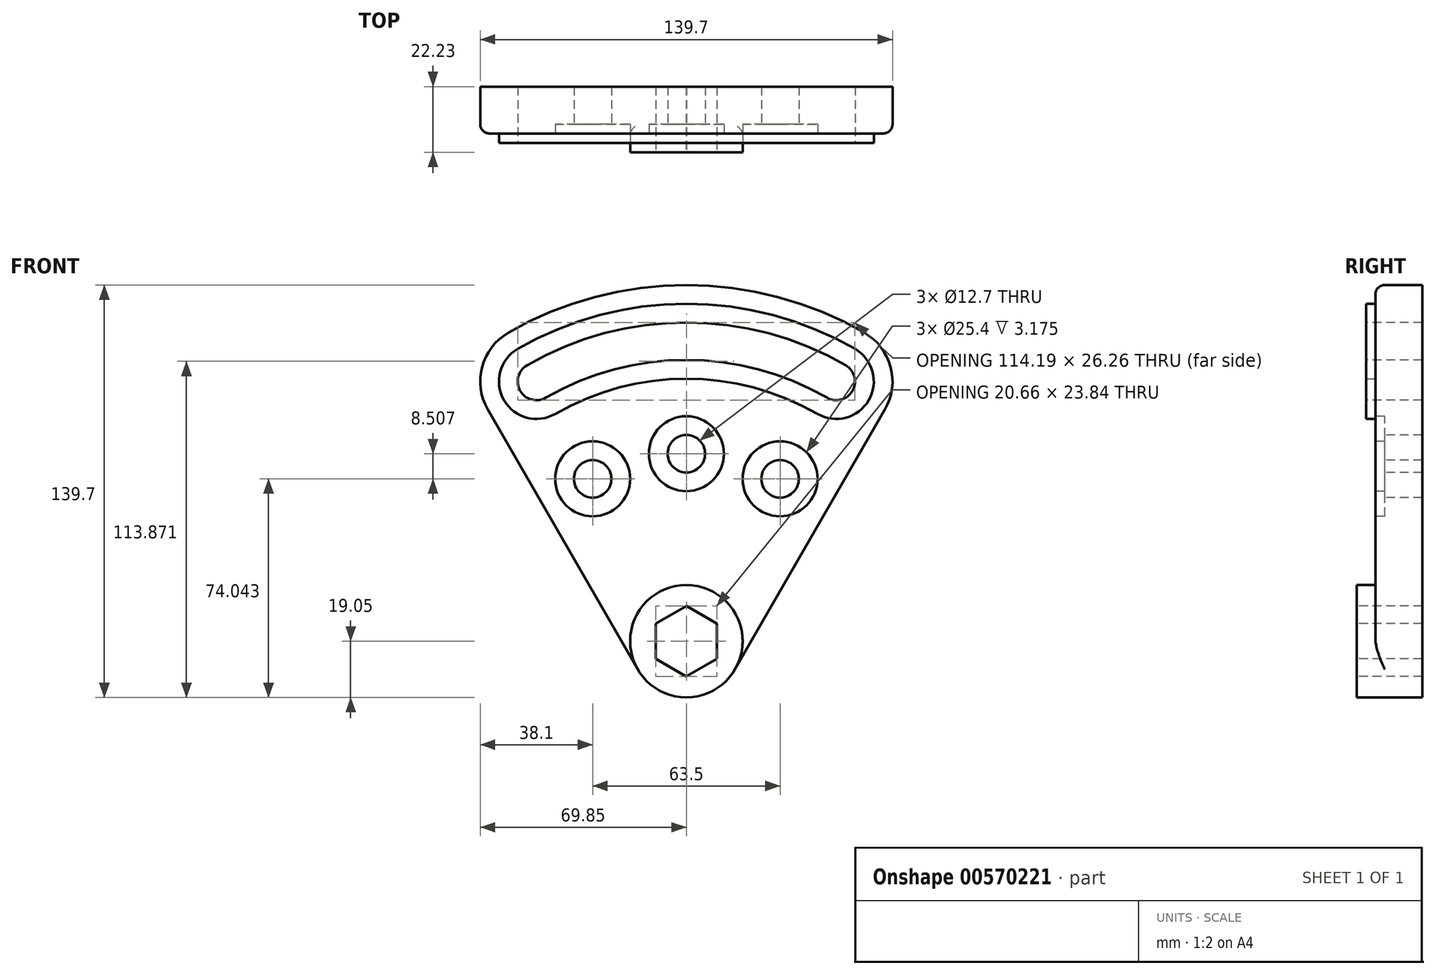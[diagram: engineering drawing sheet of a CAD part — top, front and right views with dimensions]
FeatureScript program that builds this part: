
annotation { "Feature Type Name" : "Feature", "Feature Type Description" : "" }
export const myFeature = defineFeature(function(context is Context, id is Id, definition is map)
    precondition{}
    {
        {
            var Q0;
            Q0=qCreatedBy(makeId("Front.planeOp"),FACE);
            var sketch = newSketch(context, id + "F0", { "sketchPlane" : qUnion([Q0])});
            skCircle(sketch, "E0", {"center": v(0, 0) * mm, "radius": 19.05 * mm});
            skCircle(sketch, "E1", {"center": v(0, 0) * mm, "radius": 101.6 * mm, "construction": true});
            skLineSegment(sketch, "E2", {"start": v(0, 0) * mm, "end": v(50.8, 87.99) * mm});
            skLineSegment(sketch, "E3", {"start": v(0, 0) * mm, "end": v(0, 112.62) * mm});
            skLineSegment(sketch, "E4.MirrorCS", {"start": v(0, 0) * mm, "end": v(-50.8, 87.99) * mm});
            skPoint(sketch, "E5.orphan", {"position": v(61.77, 106.98) * mm});
            skPoint(sketch, "E6.orphan", {"position": v(-61.77, 106.98) * mm});
            skArc(sketch, "E7", {"start": v(67.3, 78.46) * mm, "mid": v(69.2, 92.92) * mm, "end": v(60.33, 104.49) * mm});
            skLineSegment(sketch, "E8", {"start": v(67.3, 78.46) * mm, "end": v(16.5, -9.53) * mm});
            skArc(sketch, "E9.MirrorC", {"start": v(-67.3, 78.46) * mm, "mid": v(-69.2, 92.92) * mm, "end": v(-60.33, 104.49) * mm});
            skLineSegment(sketch, "E10.MirrorCS", {"start": v(-67.3, 78.46) * mm, "end": v(-16.5, -9.53) * mm});
            skArc(sketch, "E11", {"start": v(60.33, 104.49) * mm, "mid": v(0, 120.65) * mm, "end": v(-60.33, 104.49) * mm});
            skArc(sketch, "E12", {"start": v(-57.15, 98.99) * mm, "mid": v(-61.8, 81.64) * mm, "end": v(-44.45, 76.99) * mm});
            skArc(sketch, "E13.MirrorC", {"start": v(57.15, 98.99) * mm, "mid": v(61.8, 81.64) * mm, "end": v(44.45, 76.99) * mm});
            skCircle(sketch, "E14", {"center": v(0, 0) * mm, "radius": 63.5 * mm, "construction": true});
            skCircle(sketch, "E15", {"center": v(-31.75, 55) * mm, "radius": 6.35 * mm});
            skCircle(sketch, "E16.MirrorC", {"center": v(31.75, 55) * mm, "radius": 6.35 * mm});
            skCircle(sketch, "E17", {"center": v(0, 63.5) * mm, "radius": 6.35 * mm});
            skArc(sketch, "E18", {"start": v(57.15, 98.99) * mm, "mid": v(0, 114.3) * mm, "end": v(-57.15, 98.99) * mm});
            skArc(sketch, "E19", {"start": v(44.45, 76.99) * mm, "mid": v(0, 88.9) * mm, "end": v(-44.45, 76.99) * mm});
            skSolve(sketch);
        }
        {
            var Q0;
            Q0=makeQuery(id+"F0.imprint","IMPRINT",FACE,{"disambiguationData":[TD([[makeQuery(id+"F0.imprint","IMPRINT",EDGE,{"derivedFrom":sQuery(id+"F0.wireOp",EDGE,"E7")}),1.0]])]});
            var Q1;
            {var subQ1=sQuery(id+"F0.wireOp",EDGE,"E0");var subQ7=sQuery(id+"F0.wireOp",EDGE,"E3");var subQ11=makeQuery(id+"F0.imprint","INTERSECT",VERTEX,{"derivedFrom":[subQ1,subQ7]});Q1=makeQuery(id+"F0.imprint","IMPRINT",FACE,{"disambiguationData":[TD([[makeQuery(id+"F0.imprint","IMPRINT",EDGE,{"disambiguationData":[TD([[subQ11,-1.0]])],"derivedFrom":subQ1}),-1.0]])]});}
            var Q2;
            {var subQ5=sQuery(id+"F0.wireOp",EDGE,"E0");var subQ8=sQuery(id+"F0.wireOp",EDGE,"E3");var subQ9=makeQuery(id+"F0.imprint","INTERSECT",VERTEX,{"derivedFrom":[subQ5,subQ8]});Q2=makeQuery(id+"F0.imprint","IMPRINT",FACE,{"disambiguationData":[TD([[makeQuery(id+"F0.imprint","IMPRINT",EDGE,{"disambiguationData":[TD([[subQ9,1.0]])],"derivedFrom":subQ5}),-1.0]])]});}
            var Q3;
            {var subQ3=sQuery(id+"F0.wireOp",EDGE,"E0");var subQ6=makeQuery(id+"F0.imprint","INTERSECT",VERTEX,{"derivedFrom":[subQ3,sQuery(id+"F0.wireOp",EDGE,"E10.MirrorCS")]});Q3=makeQuery(id+"F0.imprint","IMPRINT",FACE,{"disambiguationData":[TD([[makeQuery(id+"F0.imprint","IMPRINT",EDGE,{"disambiguationData":[TD([[subQ6,1.0]])],"derivedFrom":subQ3}),1.0]])]});}
            var Q4;
            {var subQ0=sQuery(id+"F0.wireOp",EDGE,"E3");var subQ1=sQuery(id+"F0.wireOp",EDGE,"E0");var subQ2=makeQuery(id+"F0.imprint","INTERSECT",VERTEX,{"derivedFrom":[subQ1,subQ0]});Q4=makeQuery(id+"F0.imprint","IMPRINT",FACE,{"disambiguationData":[TD([[makeQuery(id+"F0.imprint","IMPRINT",EDGE,{"disambiguationData":[TD([[subQ2,-1.0]])],"derivedFrom":subQ1}),1.0]])]});}
            var Q5;
            {var subQ0=sQuery(id+"F0.wireOp",EDGE,"E3");var subQ1=sQuery(id+"F0.wireOp",EDGE,"E0");var subQ2=makeQuery(id+"F0.imprint","INTERSECT",VERTEX,{"derivedFrom":[subQ1,subQ0]});Q5=makeQuery(id+"F0.imprint","IMPRINT",FACE,{"disambiguationData":[TD([[makeQuery(id+"F0.imprint","IMPRINT",EDGE,{"disambiguationData":[TD([[subQ2,1.0]])],"derivedFrom":subQ1}),1.0]])]});}
            var Q6;
            {var subQ3=sQuery(id+"F0.wireOp",EDGE,"E12");Q6=makeQuery(id+"F0.imprint","IMPRINT",FACE,{"disambiguationData":[TD([[makeQuery(id+"F0.imprint","IMPRINT",EDGE,{"derivedFrom":subQ3}),1.0]])]});}
            extrude(context, id + "F1", {"entities" : qUnion([Q0, Q1, Q2, Q3, Q4, Q5, Q6]), "oppositeDirection" : true, "depth" : 15.88 * mm, "offsetDistance" : 25.4 * mm});
        }
        {
            var Q0;
            {var subQ3=sQuery(id+"F0.wireOp",EDGE,"E12");Q0=makeQuery(id+"F0.imprint","IMPRINT",FACE,{"disambiguationData":[TD([[makeQuery(id+"F0.imprint","IMPRINT",EDGE,{"derivedFrom":subQ3}),1.0]])]});}
            extrude(context, id + "F2", {"entities" : qUnion([Q0]), "operationType" : NewBodyOperationType.ADD, "depth" : 3.17 * mm, "offsetDistance" : 25.4 * mm});
        }
        {
            var Q0;
            {var subQ3=sQuery(id+"F0.wireOp",EDGE,"E0");var subQ6=makeQuery(id+"F0.imprint","INTERSECT",VERTEX,{"derivedFrom":[subQ3,sQuery(id+"F0.wireOp",EDGE,"E10.MirrorCS")]});Q0=makeQuery(id+"F0.imprint","IMPRINT",FACE,{"disambiguationData":[TD([[makeQuery(id+"F0.imprint","IMPRINT",EDGE,{"disambiguationData":[TD([[subQ6,1.0]])],"derivedFrom":subQ3}),1.0]])]});}
            var Q1;
            {var subQ0=sQuery(id+"F0.wireOp",EDGE,"E3");var subQ1=sQuery(id+"F0.wireOp",EDGE,"E0");var subQ2=makeQuery(id+"F0.imprint","INTERSECT",VERTEX,{"derivedFrom":[subQ1,subQ0]});Q1=makeQuery(id+"F0.imprint","IMPRINT",FACE,{"disambiguationData":[TD([[makeQuery(id+"F0.imprint","IMPRINT",EDGE,{"disambiguationData":[TD([[subQ2,-1.0]])],"derivedFrom":subQ1}),1.0]])]});}
            var Q2;
            {var subQ0=sQuery(id+"F0.wireOp",EDGE,"E3");var subQ1=sQuery(id+"F0.wireOp",EDGE,"E0");var subQ2=makeQuery(id+"F0.imprint","INTERSECT",VERTEX,{"derivedFrom":[subQ1,subQ0]});Q2=makeQuery(id+"F0.imprint","IMPRINT",FACE,{"disambiguationData":[TD([[makeQuery(id+"F0.imprint","IMPRINT",EDGE,{"disambiguationData":[TD([[subQ2,1.0]])],"derivedFrom":subQ1}),1.0]])]});}
            extrude(context, id + "F3", {"entities" : qUnion([Q0, Q1, Q2]), "operationType" : NewBodyOperationType.ADD, "depth" : 6.35 * mm, "offsetDistance" : 25.4 * mm});
        }
        {
            var Q0;
            Q0=makeQuery(id+"F2.opExtrude","CAP_FACE",FACE,{"disambiguationData":[OSD([sQuery(id+"F0.wireOp",EDGE,"E12"),sQuery(id+"F0.wireOp",EDGE,"E13.MirrorC"),sQuery(id+"F0.wireOp",EDGE,"E18"),sQuery(id+"F0.wireOp",EDGE,"E19")])],"isStart":false});
            var sketch = newSketch(context, id + "F4", { "sketchPlane" : qUnion([Q0])});
            skArc(sketch, "E20", {"start": v(-53.98, 93.49) * mm, "mid": v(-56.3, 84.81) * mm, "end": v(-47.63, 82.49) * mm});
            skArc(sketch, "E21", {"start": v(47.63, 82.49) * mm, "mid": v(56.3, 84.81) * mm, "end": v(53.98, 93.49) * mm});
            skArc(sketch, "E22", {"start": v(53.98, 93.49) * mm, "mid": v(0, 107.95) * mm, "end": v(-53.98, 93.49) * mm});
            skArc(sketch, "E23", {"start": v(47.63, 82.49) * mm, "mid": v(0, 95.25) * mm, "end": v(-47.63, 82.49) * mm});
            skSolve(sketch);
        }
        {
            var Q0;
            Q0=makeQuery(id+"F4.imprint","IMPRINT",FACE,{"disambiguationData":[TD([[makeQuery(id+"F4.imprint","IMPRINT",EDGE,{"derivedFrom":sQuery(id+"F4.wireOp",EDGE,"E20")}),1.0]])]});
            extrude(context, id + "F5", {"entities" : qUnion([Q0]), "operationType" : NewBodyOperationType.REMOVE, "oppositeDirection" : true, "depth" : 50.8 * mm, "offsetDistance" : 25.4 * mm});
        }
        {
            var Q0;
            Q0=makeQuery(id+"F1.opExtrude","CAP_FACE",FACE,{"disambiguationData":[OSD([sQuery(id+"F0.wireOp",EDGE,"E0"),sQuery(id+"F0.wireOp",EDGE,"E7"),sQuery(id+"F0.wireOp",EDGE,"E8"),sQuery(id+"F0.wireOp",EDGE,"E9.MirrorC"),sQuery(id+"F0.wireOp",EDGE,"E10.MirrorCS"),sQuery(id+"F0.wireOp",EDGE,"E11"),sQuery(id+"F0.wireOp",EDGE,"E15"),sQuery(id+"F0.wireOp",EDGE,"E16.MirrorC"),sQuery(id+"F0.wireOp",EDGE,"E17")])],"isStart":true});
            var sketch = newSketch(context, id + "F6", { "sketchPlane" : qUnion([Q0])});
            skCircle(sketch, "E24", {"center": v(-31.75, 55) * mm, "radius": 12.7 * mm});
            skCircle(sketch, "E25", {"center": v(0, 63.5) * mm, "radius": 12.7 * mm});
            skCircle(sketch, "E26", {"center": v(31.75, 55) * mm, "radius": 12.7 * mm});
            skSolve(sketch);
        }
        {
            var Q0;
            Q0=makeQuery(id+"F6.imprint","IMPRINT",FACE,{"disambiguationData":[TD([[makeQuery(id+"F6.imprint","IMPRINT",EDGE,{"derivedFrom":sQuery(id+"F6.wireOp",EDGE,"E24")}),1.0]])]});
            var Q1;
            Q1=makeQuery(id+"F6.imprint","IMPRINT",FACE,{"disambiguationData":[TD([[makeQuery(id+"F6.imprint","IMPRINT",EDGE,{"derivedFrom":sQuery(id+"F6.wireOp",EDGE,"E25")}),1.0]])]});
            var Q2;
            Q2=makeQuery(id+"F6.imprint","IMPRINT",FACE,{"disambiguationData":[TD([[makeQuery(id+"F6.imprint","IMPRINT",EDGE,{"derivedFrom":sQuery(id+"F6.wireOp",EDGE,"E26")}),1.0]])]});
            extrude(context, id + "F7", {"entities" : qUnion([Q0, Q1, Q2]), "operationType" : NewBodyOperationType.REMOVE, "oppositeDirection" : true, "depth" : 3.17 * mm, "offsetDistance" : 25.4 * mm});
        }
        {
            var Q0;
            Q0=makeQuery(id+"F3.opExtrude","CAP_FACE",FACE,{"disambiguationData":[OSD([sQuery(id+"F0.wireOp",EDGE,"E0")])],"isStart":false});
            var sketch = newSketch(context, id + "F8", { "sketchPlane" : qUnion([Q0])});
            skCircle(sketch, "E27.cCircle", {"center": v(0, 0) * mm, "radius": 10.33 * mm, "construction": true});
            skLineSegment(sketch, "E27.0", {"start": v(-0.01, -11.92) * mm, "end": v(-10.33, -5.95) * mm});
            skLineSegment(sketch, "E27.1", {"start": v(-10.33, -5.95) * mm, "end": v(-10.32, 5.97) * mm});
            skLineSegment(sketch, "E27.2", {"start": v(-10.32, 5.97) * mm, "end": v(0.01, 11.92) * mm});
            skLineSegment(sketch, "E27.3", {"start": v(0.01, 11.92) * mm, "end": v(10.33, 5.95) * mm});
            skLineSegment(sketch, "E27.4", {"start": v(10.33, 5.95) * mm, "end": v(10.32, -5.97) * mm});
            skLineSegment(sketch, "E27.5", {"start": v(10.32, -5.97) * mm, "end": v(-0.01, -11.92) * mm});
            skPoint(sketch, "E27.0.midPoint", {"position": v(-5.17, -8.94) * mm});
            skSolve(sketch);
        }
        {
            var Q0;
            Q0=makeQuery(id+"F8.imprint","IMPRINT",FACE,{"disambiguationData":[TD([[makeQuery(id+"F8.imprint","IMPRINT",EDGE,{"derivedFrom":sQuery(id+"F8.wireOp",EDGE,"E27.0")}),-1.0]])]});
            extrude(context, id + "F9", {"entities" : qUnion([Q0]), "operationType" : NewBodyOperationType.REMOVE, "oppositeDirection" : true, "depth" : 25.4 * mm, "offsetDistance" : 25.4 * mm});
        }
        {
            var Q0;
            Q0=makeQuery(id+"F1.opExtrude","CAP_EDGE",EDGE,{"disambiguationData":[OSD([sQuery(id+"F0.wireOp",EDGE,"E10.MirrorCS")])],"isStart":true});
            var Q1;
            Q1=makeQuery(id+"F3.opExtrude","CAP_EDGE",EDGE,{"disambiguationData":[OSD([sQuery(id+"F0.wireOp",EDGE,"E0")])],"isStart":true});
            var Q2;
            Q2=makeQuery(id+"F2.opExtrude","CAP_EDGE",EDGE,{"disambiguationData":[OSD([sQuery(id+"F0.wireOp",EDGE,"E19")])],"isStart":true});
            var Q3;
            Q3=makeQuery(id+"F2.opExtrude","CAP_EDGE",EDGE,{"disambiguationData":[OSD([sQuery(id+"F0.wireOp",EDGE,"E12")])],"isStart":true});
            var Q4;
            Q4=makeQuery(id+"F2.opExtrude","CAP_EDGE",EDGE,{"disambiguationData":[OSD([sQuery(id+"F0.wireOp",EDGE,"E13.MirrorC")])],"isStart":true});
            var Q5;
            Q5=makeQuery(id+"F2.opExtrude","CAP_EDGE",EDGE,{"disambiguationData":[OSD([sQuery(id+"F0.wireOp",EDGE,"E18")])],"isStart":true});
            var Q6;
            Q6=makeQuery(id+"F1.opExtrude","CAP_EDGE",EDGE,{"disambiguationData":[OSD([sQuery(id+"F0.wireOp",EDGE,"E11")])],"isStart":true});
            var Q7;
            Q7=makeQuery(id+"F1.opExtrude","CAP_EDGE",EDGE,{"disambiguationData":[OSD([sQuery(id+"F0.wireOp",EDGE,"E7")])],"isStart":true});
            var Q8;
            Q8=makeQuery(id+"F1.opExtrude","CAP_EDGE",EDGE,{"disambiguationData":[OSD([sQuery(id+"F0.wireOp",EDGE,"E9.MirrorC")])],"isStart":true});
            fillet(context, id + "F10", {"entities" : qUnion([Q0, Q1, Q2, Q3, Q4, Q5, Q6, Q7, Q8]), "radius" : 3.17 * mm, "tangentPropagation" : true, "allowEdgeOverflow" : false});
        }
    });
